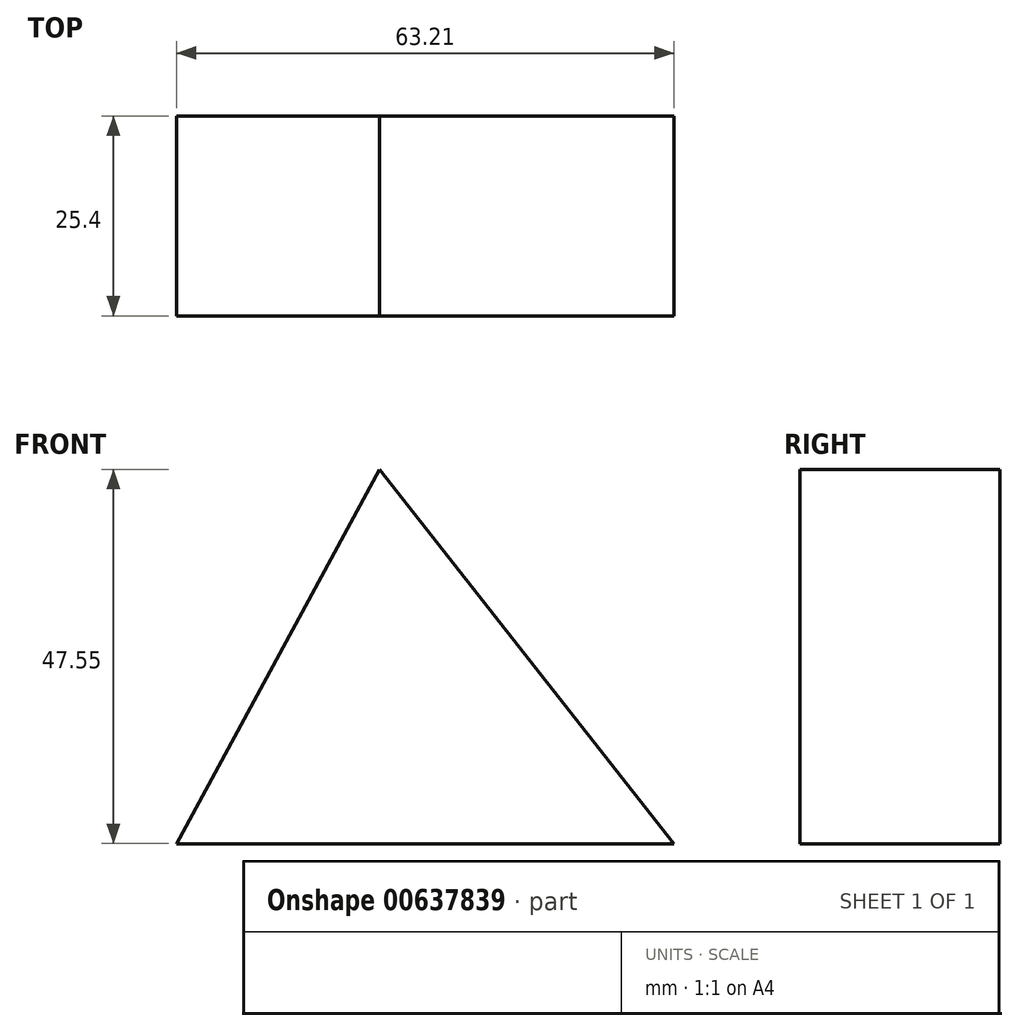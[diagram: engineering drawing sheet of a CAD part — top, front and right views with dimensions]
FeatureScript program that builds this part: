
annotation { "Feature Type Name" : "Feature", "Feature Type Description" : "" }
export const myFeature = defineFeature(function(context is Context, id is Id, definition is map)
    precondition{}
    {
        {
            var Q0;
            Q0=qCreatedBy(makeId("Front.planeOp"),FACE);
            var sketch = newSketch(context, id + "F0", { "sketchPlane" : qUnion([Q0])});
            skLineSegment(sketch, "E0", {"start": v(-41.34, 62.35) * mm, "end": v(-67.12, 14.8) * mm});
            skLineSegment(sketch, "E1", {"start": v(-67.12, 14.8) * mm, "end": v(-3.91, 14.8) * mm});
            skLineSegment(sketch, "E2", {"start": v(-3.91, 14.8) * mm, "end": v(-41.34, 62.35) * mm});
            skSolve(sketch);
        }
        {
            var Q0;
            Q0 = qSketchRegion(id + "F0", true);
            extrude(context, id + "F1", {"entities" : qUnion([Q0]), "depth" : 25.4 * mm, "offsetDistance" : 25.4 * mm});
        }
    });
